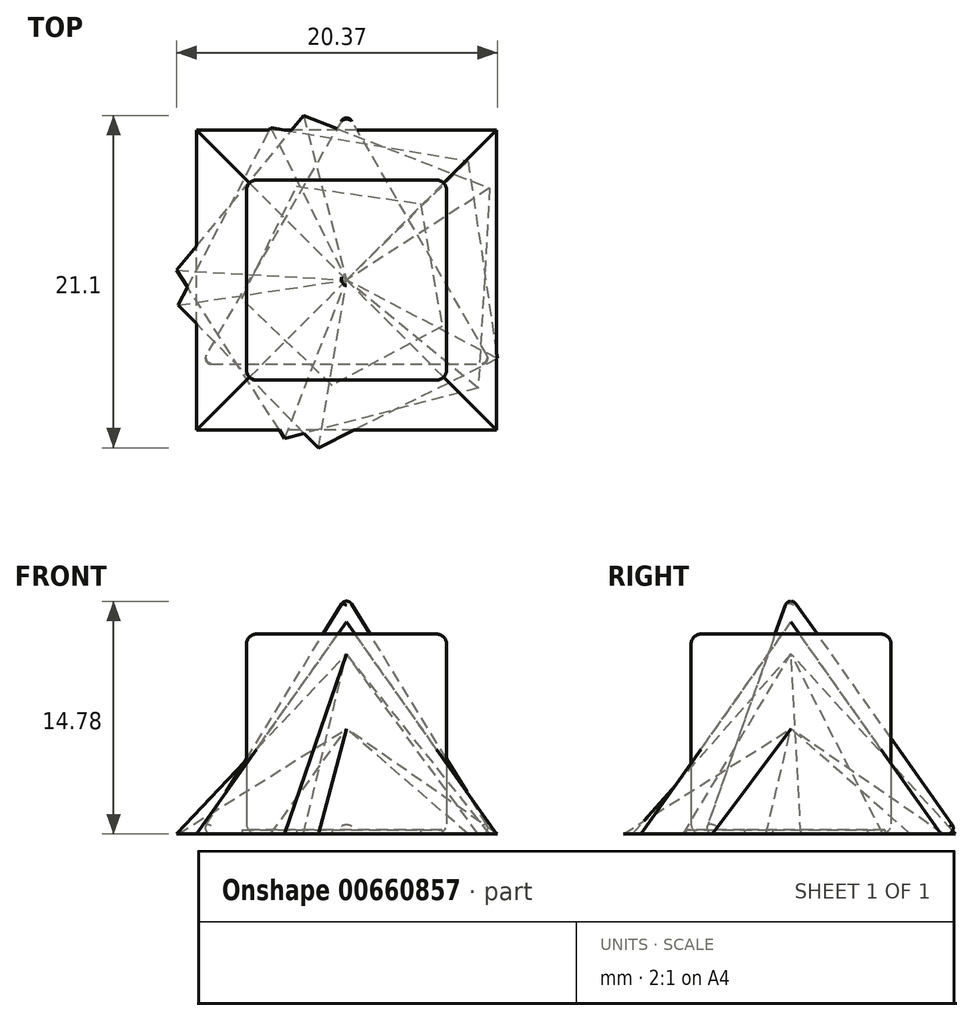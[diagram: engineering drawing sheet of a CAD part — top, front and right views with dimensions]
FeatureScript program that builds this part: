
annotation { "Feature Type Name" : "Feature", "Feature Type Description" : "" }
export const myFeature = defineFeature(function(context is Context, id is Id, definition is map)
    precondition{}
    {
        {
            var Q0;
            Q0=qCreatedBy(makeId("Top.planeOp"),FACE);
            var sketch = newSketch(context, id + "F0", { "sketchPlane" : qUnion([Q0])});
            skCircle(sketch, "E0.cCircle", {"center": v(0, 0) * mm, "radius": 10.8 * mm, "construction": true});
            skLineSegment(sketch, "E0.0", {"start": v(9.58, -5) * mm, "end": v(-1.8, -10.65) * mm});
            skLineSegment(sketch, "E0.1", {"start": v(-1.8, -10.65) * mm, "end": v(-10.69, -1.59) * mm});
            skLineSegment(sketch, "E0.2", {"start": v(-10.69, -1.59) * mm, "end": v(-4.81, 9.67) * mm});
            skLineSegment(sketch, "E0.3", {"start": v(-4.81, 9.67) * mm, "end": v(7.71, 7.57) * mm});
            skLineSegment(sketch, "E0.4", {"start": v(7.71, 7.57) * mm, "end": v(9.58, -5) * mm});
            skSolve(sketch);
        }
        {
            var Q0;
            Q0=qCreatedBy(makeId("Front.planeOp"),FACE);
            var sketch = newSketch(context, id + "F1", { "sketchPlane" : qUnion([Q0])});
            skLineSegment(sketch, "E1", {"start": v(0, 0) * mm, "end": v(0, 6.68) * mm});
            skSolve(sketch);
        }
        {
            var Q0;
            Q0=makeQuery(id+"F0.imprint","IMPRINT",FACE,{"disambiguationData":[TD([[makeQuery(id+"F0.imprint","IMPRINT",EDGE,{"derivedFrom":sQuery(id+"F0.wireOp",EDGE,"E0.0")}),-1.0]])]});
            var Q1;
            Q1=sQuery(id+"F1.wireOp",VERTEX,"E1.end");
            loft(context, id + "F2", {"sheetProfilesArray" : [{ "sheetProfileEntities" : qUnion([Q0]) }, { "sheetProfileEntities" : qUnion([Q1]) }]});
        }
        {
            var Q0;
            Q0=qCreatedBy(makeId("Top.planeOp"),FACE);
            var sketch = newSketch(context, id + "F3", { "sketchPlane" : qUnion([Q0])});
            skLineSegment(sketch, "E2", {"start": v(0, 11) * mm, "end": v(9.52, -5.5) * mm});
            skLineSegment(sketch, "E3", {"start": v(9.53, -5.5) * mm, "end": v(-9.52, -5.5) * mm});
            skLineSegment(sketch, "E4", {"start": v(-9.52, -5.5) * mm, "end": v(0, 11) * mm});
            skLineSegment(sketch, "E5", {"start": v(0, -5.5) * mm, "end": v(0, 0) * mm, "construction": true});
            skLineSegment(sketch, "E6", {"start": v(-4.76, 2.75) * mm, "end": v(0, 0) * mm, "construction": true});
            skLineSegment(sketch, "E7", {"start": v(4.76, 2.75) * mm, "end": v(0, 0) * mm, "construction": true});
            skSolve(sketch);
        }
        {
            var Q0;
            Q0=qCreatedBy(makeId("Front.planeOp"),FACE);
            var sketch = newSketch(context, id + "F4", { "sketchPlane" : qUnion([Q0])});
            skLineSegment(sketch, "E8", {"start": v(0, 0) * mm, "end": v(0, 15.54) * mm});
            skSolve(sketch);
        }
        {
            var Q0;
            Q0=makeQuery(id+"F3.imprint","IMPRINT",FACE,{"disambiguationData":[TD([[makeQuery(id+"F3.imprint","IMPRINT",EDGE,{"derivedFrom":sQuery(id+"F3.wireOp",EDGE,"E2")}),-1.0]])]});
            var Q1;
            Q1=sQuery(id+"F4.wireOp",VERTEX,"E8.end");
            loft(context, id + "F5", {"sheetProfilesArray" : [{ "sheetProfileEntities" : qUnion([Q0]) }, { "sheetProfileEntities" : qUnion([Q1]) }]});
        }
        {
            var Q0;
            Q0=qCreatedBy(makeId("Top.planeOp"),FACE);
            var sketch = newSketch(context, id + "F6", { "sketchPlane" : qUnion([Q0])});
            skLineSegment(sketch, "E9.bottom", {"start": v(-6.35, 6.35) * mm, "end": v(6.35, 6.35) * mm});
            skLineSegment(sketch, "E9.top", {"start": v(-6.35, -6.35) * mm, "end": v(6.35, -6.35) * mm});
            skLineSegment(sketch, "E9.left", {"start": v(-6.35, 6.35) * mm, "end": v(-6.35, -6.35) * mm});
            skLineSegment(sketch, "E9.right", {"start": v(6.35, 6.35) * mm, "end": v(6.35, -6.35) * mm});
            skPoint(sketch, "E9.middle", {"position": v(0, 0) * mm});
            skSolve(sketch);
        }
        {
            var Q0;
            Q0 = qSketchRegion(id + "F6", true);
            extrude(context, id + "F7", {"entities" : qUnion([Q0]), "depth" : 12.7 * mm, "offsetDistance" : 25.4 * mm});
        }
        {
            var Q0;
            Q0=makeQuery(id+"F7.opExtrude","CAP_EDGE",EDGE,{"disambiguationData":[OSD([sQuery(id+"F6.wireOp",EDGE,"E9.right")])],"isStart":false});
            var Q1;
            Q1=makeQuery(id+"F7.opExtrude","CAP_EDGE",EDGE,{"disambiguationData":[OSD([sQuery(id+"F6.wireOp",EDGE,"E9.right")])],"isStart":true});
            var Q2;
            Q2=makeQuery(id+"F7.opExtrude","SWEPT_EDGE",EDGE,{"disambiguationData":[OSD([sQuery(id+"F6.wireOp",EDGE,"E9.bottom"),sQuery(id+"F6.wireOp",EDGE,"E9.right")])]});
            var Q3;
            Q3=makeQuery(id+"F7.opExtrude","SWEPT_EDGE",EDGE,{"disambiguationData":[OSD([sQuery(id+"F6.wireOp",EDGE,"E9.top"),sQuery(id+"F6.wireOp",EDGE,"E9.right")])]});
            var Q4;
            Q4=makeQuery(id+"F7.opExtrude","CAP_EDGE",EDGE,{"disambiguationData":[OSD([sQuery(id+"F6.wireOp",EDGE,"E9.bottom")])],"isStart":false});
            var Q5;
            Q5=makeQuery(id+"F7.opExtrude","CAP_EDGE",EDGE,{"disambiguationData":[OSD([sQuery(id+"F6.wireOp",EDGE,"E9.top")])],"isStart":false});
            var Q6;
            Q6=makeQuery(id+"F7.opExtrude","CAP_EDGE",EDGE,{"disambiguationData":[OSD([sQuery(id+"F6.wireOp",EDGE,"E9.top")])],"isStart":true});
            var Q7;
            Q7=makeQuery(id+"F7.opExtrude","CAP_EDGE",EDGE,{"disambiguationData":[OSD([sQuery(id+"F6.wireOp",EDGE,"E9.bottom")])],"isStart":true});
            var Q8;
            Q8=makeQuery(id+"F7.opExtrude","SWEPT_EDGE",EDGE,{"disambiguationData":[OSD([sQuery(id+"F6.wireOp",EDGE,"E9.top"),sQuery(id+"F6.wireOp",EDGE,"E9.left")])]});
            var Q9;
            Q9=makeQuery(id+"F7.opExtrude","SWEPT_FACE",FACE,{"disambiguationData":[OSD([sQuery(id+"F6.wireOp",EDGE,"E9.left")])]});
            fillet(context, id + "F8", {"entities" : qUnion([Q0, Q1, Q2, Q3, Q4, Q5, Q6, Q7, Q8, Q9]), "radius" : 0.64 * mm, "tangentPropagation" : true, "allowEdgeOverflow" : false});
        }
        {
            var Q0;
            Q0=makeQuery(id+"F5.opLoft","SWEPT_EDGE",EDGE,{"disambiguationData":[OSD([sQuery(id+"F3.wireOp",EDGE,"E3"),sQuery(id+"F3.wireOp",EDGE,"E4"),sQuery(id+"F4.wireOp",VERTEX,"E8.end")])]});
            var Q1;
            Q1=makeQuery(id+"F5.opLoft","SWEPT_EDGE",EDGE,{"disambiguationData":[OSD([sQuery(id+"F3.wireOp",EDGE,"E2"),sQuery(id+"F3.wireOp",EDGE,"E3"),sQuery(id+"F4.wireOp",VERTEX,"E8.end")])]});
            var Q2;
            Q2=makeQuery(id+"F5.opLoft","SWEPT_EDGE",EDGE,{"disambiguationData":[OSD([sQuery(id+"F3.wireOp",EDGE,"E2"),sQuery(id+"F3.wireOp",EDGE,"E4"),sQuery(id+"F4.wireOp",VERTEX,"E8.end")])]});
            var Q3;
            {var subQ0=sQuery(id+"F3.wireOp",EDGE,"E3");var subQ1=sQuery(id+"F3.wireOp",EDGE,"E4");var subQ2=sQuery(id+"F3.wireOp",EDGE,"E2");Q3=makeQuery(id+"F5.opLoft","MID_CAP_EDGE",EDGE,{"disambiguationData":[OSD([subQ2,subQ0,subQ1]),TDD([makeQuery(id+"F3.imprint","INTERSECT",VERTEX,{"derivedFrom":[subQ2,subQ0]}),makeQuery(id+"F3.imprint","INTERSECT",VERTEX,{"derivedFrom":[subQ0,subQ1]}),makeQuery(id+"F3.imprint","IMPRINT",EDGE,{"derivedFrom":subQ0})])],"capPos":0.0});}
            var Q4;
            {var subQ0=sQuery(id+"F3.wireOp",EDGE,"E2");var subQ1=sQuery(id+"F3.wireOp",EDGE,"E3");var subQ2=sQuery(id+"F3.wireOp",EDGE,"E4");Q4=makeQuery(id+"F5.opLoft","MID_CAP_EDGE",EDGE,{"disambiguationData":[OSD([subQ0,subQ1,subQ2]),TDD([makeQuery(id+"F3.imprint","INTERSECT",VERTEX,{"derivedFrom":[subQ0,subQ2]}),makeQuery(id+"F3.imprint","INTERSECT",VERTEX,{"derivedFrom":[subQ0,subQ1]}),makeQuery(id+"F3.imprint","IMPRINT",EDGE,{"derivedFrom":subQ0})])],"capPos":0.0});}
            var Q5;
            {var subQ0=sQuery(id+"F3.wireOp",EDGE,"E4");var subQ1=sQuery(id+"F3.wireOp",EDGE,"E3");var subQ2=sQuery(id+"F3.wireOp",EDGE,"E2");Q5=makeQuery(id+"F5.opLoft","MID_CAP_EDGE",EDGE,{"disambiguationData":[OSD([subQ2,subQ1,subQ0]),TDD([makeQuery(id+"F3.imprint","INTERSECT",VERTEX,{"derivedFrom":[subQ2,subQ0]}),makeQuery(id+"F3.imprint","INTERSECT",VERTEX,{"derivedFrom":[subQ1,subQ0]}),makeQuery(id+"F3.imprint","IMPRINT",EDGE,{"derivedFrom":subQ0})])],"capPos":0.0});}
            fillet(context, id + "F9", {"entities" : qUnion([Q0, Q1, Q2, Q3, Q4, Q5]), "radius" : 0.38 * mm, "tangentPropagation" : true, "allowEdgeOverflow" : false});
        }
        {
            var Q0;
            Q0=qCreatedBy(makeId("Top.planeOp"),FACE);
            var sketch = newSketch(context, id + "F10", { "sketchPlane" : qUnion([Q0])});
            skLineSegment(sketch, "E10.bottom", {"start": v(9.53, -9.53) * mm, "end": v(-9.53, -9.53) * mm});
            skLineSegment(sketch, "E10.top", {"start": v(9.53, 9.53) * mm, "end": v(-9.53, 9.53) * mm});
            skLineSegment(sketch, "E10.left", {"start": v(9.53, -9.53) * mm, "end": v(9.53, 9.53) * mm});
            skLineSegment(sketch, "E10.right", {"start": v(-9.53, -9.53) * mm, "end": v(-9.53, 9.53) * mm});
            skPoint(sketch, "E10.middle", {"position": v(0, 0) * mm});
            skSolve(sketch);
        }
        {
            var Q0;
            Q0=qCreatedBy(makeId("Front.planeOp"),FACE);
            var sketch = newSketch(context, id + "F11", { "sketchPlane" : qUnion([Q0])});
            skLineSegment(sketch, "E11", {"start": v(0, 0) * mm, "end": v(0, 13.46) * mm});
            skSolve(sketch);
        }
        {
            var Q0;
            Q0=makeQuery(id+"F10.imprint","IMPRINT",FACE,{"disambiguationData":[TD([[makeQuery(id+"F10.imprint","IMPRINT",EDGE,{"derivedFrom":sQuery(id+"F10.wireOp",EDGE,"E10.bottom")}),-1.0]])]});
            var Q1;
            Q1=sQuery(id+"F11.wireOp",VERTEX,"E11.end");
            loft(context, id + "F12", {"sheetProfilesArray" : [{ "sheetProfileEntities" : qUnion([Q0]) }, { "sheetProfileEntities" : qUnion([Q1]) }]});
        }
        {
            var Q0;
            Q0=qCreatedBy(makeId("Top.planeOp"),FACE);
            var sketch = newSketch(context, id + "F13", { "sketchPlane" : qUnion([Q0])});
            skCircle(sketch, "E12.cCircle", {"center": v(0, 0) * mm, "radius": 6.75 * mm, "construction": true});
            skLineSegment(sketch, "E12.0", {"start": v(6.07, -2.95) * mm, "end": v(-0.93, -6.69) * mm});
            skLineSegment(sketch, "E12.1", {"start": v(-0.93, -6.69) * mm, "end": v(-6.65, -1.18) * mm});
            skLineSegment(sketch, "E12.2", {"start": v(-6.65, -1.18) * mm, "end": v(-3.18, 5.96) * mm});
            skLineSegment(sketch, "E12.3", {"start": v(-3.18, 5.96) * mm, "end": v(4.68, 4.86) * mm});
            skLineSegment(sketch, "E12.4", {"start": v(4.68, 4.86) * mm, "end": v(6.07, -2.95) * mm});
            skSolve(sketch);
        }
        {
            var Q0;
            Q0=makeQuery(id+"F13.imprint","IMPRINT",FACE,{"disambiguationData":[TD([[makeQuery(id+"F13.imprint","IMPRINT",EDGE,{"derivedFrom":sQuery(id+"F13.wireOp",EDGE,"E12.0")}),-1.0]])]});
            extrude(context, id + "F14", {"entities" : qUnion([Q0]), "depth" : 0.25 * mm, "offsetDistance" : 25.4 * mm});
        }
        {
            var Q0;
            Q0=qCreatedBy(makeId("Top.planeOp"),FACE);
            var sketch = newSketch(context, id + "F15", { "sketchPlane" : qUnion([Q0])});
            skLineSegment(sketch, "E13", {"start": v(0, -7.17) * mm, "end": v(5.71, -5.1) * mm});
            skLineSegment(sketch, "E14", {"start": v(5.71, -5.1) * mm, "end": v(0, 8.7) * mm});
            skLineSegment(sketch, "E15", {"start": v(0, 8.7) * mm, "end": v(-5.72, -5.1) * mm});
            skLineSegment(sketch, "E16", {"start": v(-5.72, -5.1) * mm, "end": v(0, -7.17) * mm});
            skLineSegment(sketch, "E17", {"start": v(6.36, -7.17) * mm, "end": v(-7.81, -7.17) * mm, "construction": true});
            skLineSegment(sketch, "E18", {"start": v(-11.76, 8.7) * mm, "end": v(17.64, 8.7) * mm, "construction": true});
            skSolve(sketch);
        }
        {
            var Q0;
            Q0 = qSketchRegion(id + "F15", true);
            var Q1;
            Q1=makeQuery(id+"F15.imprint","IMPRINT",FACE,{"disambiguationData":[TD([[makeQuery(id+"F15.imprint","IMPRINT",EDGE,{"derivedFrom":sQuery(id+"F15.wireOp",EDGE,"E13")}),1.0]])]});
            extrude(context, id + "F16", {"entities" : qUnion([Q0, Q1]), "depth" : 0.25 * mm, "offsetDistance" : 25.4 * mm});
        }
        {
            var Q0;
            Q0=qCreatedBy(makeId("Top.planeOp"),FACE);
            var sketch = newSketch(context, id + "F17", { "sketchPlane" : qUnion([Q0])});
            skCircle(sketch, "E19.cCircle", {"center": v(0, 0) * mm, "radius": 10.8 * mm, "construction": true});
            skLineSegment(sketch, "E19.0", {"start": v(8.36, -6.84) * mm, "end": v(-3.92, -10.07) * mm});
            skLineSegment(sketch, "E19.1", {"start": v(-3.92, -10.07) * mm, "end": v(-10.79, 0.62) * mm});
            skLineSegment(sketch, "E19.2", {"start": v(-10.79, 0.62) * mm, "end": v(-2.74, 10.45) * mm});
            skLineSegment(sketch, "E19.3", {"start": v(-2.74, 10.45) * mm, "end": v(9.1, 5.84) * mm});
            skLineSegment(sketch, "E19.4", {"start": v(9.1, 5.84) * mm, "end": v(8.36, -6.84) * mm});
            skSolve(sketch);
        }
        {
            var Q0;
            Q0=qCreatedBy(makeId("Front.planeOp"),FACE);
            var sketch = newSketch(context, id + "F18", { "sketchPlane" : qUnion([Q0])});
            skLineSegment(sketch, "E20", {"start": v(0, 0) * mm, "end": v(0, 11.43) * mm});
            skSolve(sketch);
        }
        {
            var Q0;
            Q0=makeQuery(id+"F17.imprint","IMPRINT",FACE,{"disambiguationData":[TD([[makeQuery(id+"F17.imprint","IMPRINT",EDGE,{"derivedFrom":sQuery(id+"F17.wireOp",EDGE,"E19.0")}),-1.0]])]});
            var Q1;
            Q1=sQuery(id+"F18.wireOp",VERTEX,"E20.end");
            var Q2;
            Q2=makeQuery(id+"F17.imprint","IMPRINT",FACE,{"disambiguationData":[TD([[makeQuery(id+"F17.imprint","IMPRINT",EDGE,{"derivedFrom":sQuery(id+"F17.wireOp",EDGE,"E19.0")}),-1.0]])]});
            loft(context, id + "F19", {"sheetProfilesArray" : [{ "sheetProfileEntities" : qUnion([Q0]) }, { "sheetProfileEntities" : qUnion([Q1]) }], "wireProfilesArray" : [{ "wireProfileEntities" : qUnion([Q2]) }]});
        }
        {
            var Q0;
            Q0=makeQuery(id+"F16.opExtrude","SWEPT_BODY",BODY,{"disambiguationData":[OSD([sQuery(id+"F15.wireOp",EDGE,"E13"),sQuery(id+"F15.wireOp",EDGE,"E14"),sQuery(id+"F15.wireOp",EDGE,"E15"),sQuery(id+"F15.wireOp",EDGE,"E16")])]});
            deleteBodies(context, id + "F20", {"entities" : qUnion([Q0])});
        }
    });
